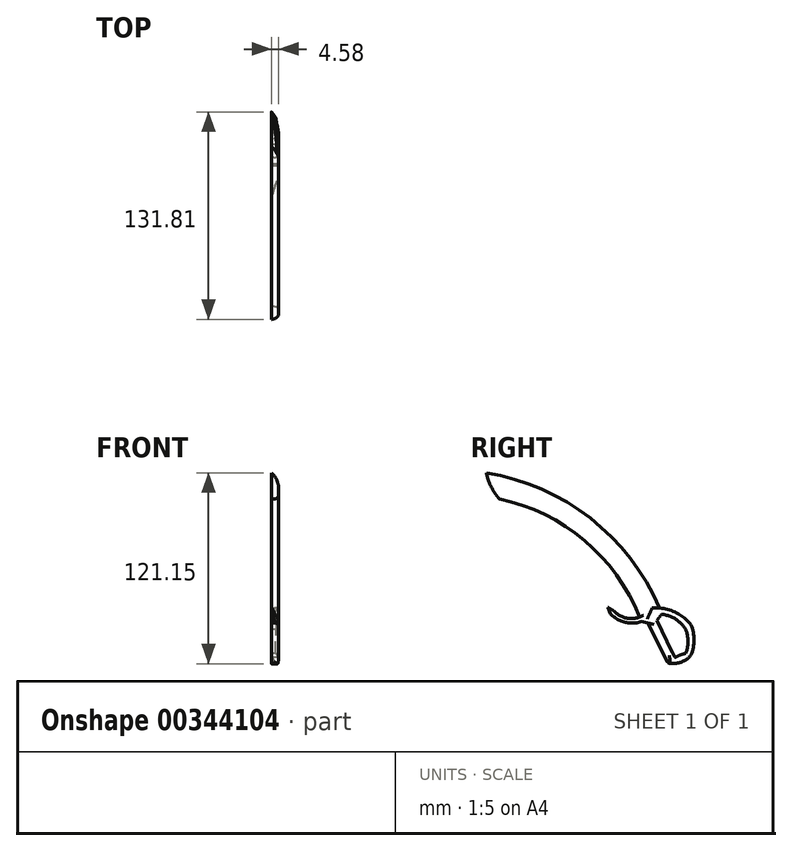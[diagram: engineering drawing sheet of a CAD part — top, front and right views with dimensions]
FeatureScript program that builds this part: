
annotation { "Feature Type Name" : "Feature", "Feature Type Description" : "" }
export const myFeature = defineFeature(function(context is Context, id is Id, definition is map)
    precondition{}
    {
        {
            var Q0;
            Q0=qCreatedBy(makeId("Right.planeOp"),FACE);
            var sketch = newSketch(context, id + "F0", { "sketchPlane" : qUnion([Q0])});
            skArc(sketch, "E0", {"start": v(55.77, -25.1) * mm, "mid": v(11.84, 31.93) * mm, "end": v(-54.16, 60.68) * mm});
            skArc(sketch, "E1", {"start": v(43.15, -30.87) * mm, "mid": v(8.04, 17.8) * mm, "end": v(-45.88, 44.15) * mm});
            skArc(sketch, "E2", {"start": v(26.88, -27.02) * mm, "mid": v(34.43, -31.4) * mm, "end": v(43.15, -30.87) * mm});
            skArc(sketch, "E3", {"start": v(24.68, -28.79) * mm, "mid": v(33.82, -34.17) * mm, "end": v(44.41, -33.72) * mm});
            skLineSegment(sketch, "E4", {"start": v(44.41, -33.72) * mm, "end": v(48.52, -34.67) * mm});
            skLineSegment(sketch, "E5", {"start": v(48.52, -34.67) * mm, "end": v(60.52, -58.92) * mm});
            skLineSegment(sketch, "E6", {"start": v(57.04, -29.15) * mm, "end": v(54.22, -32.9) * mm});
            skLineSegment(sketch, "E7", {"start": v(54.22, -32.9) * mm, "end": v(65.62, -56.63) * mm});
            skLineSegment(sketch, "E8", {"start": v(24.68, -28.79) * mm, "end": v(23.2, -24.76) * mm});
            skLineSegment(sketch, "E9", {"start": v(23.2, -24.76) * mm, "end": v(26.88, -27.02) * mm});
            skArc(sketch, "E10", {"start": v(60.52, -58.92) * mm, "mid": v(64.17, -60.23) * mm, "end": v(65.62, -56.63) * mm});
            skArc(sketch, "E11", {"start": v(-54.16, 60.68) * mm, "mid": v(-51.15, 51.85) * mm, "end": v(-45.88, 44.15) * mm});
            skArc(sketch, "E12", {"start": v(49.46, -27.99) * mm, "mid": v(8.46, 23.66) * mm, "end": v(-51.15, 51.85) * mm});
            skLineSegment(sketch, "E13", {"start": v(55.77, -25.1) * mm, "end": v(43.15, -30.87) * mm});
            skArc(sketch, "E14", {"start": v(72.45, -38.84) * mm, "mid": v(65.93, -32.1) * mm, "end": v(57.04, -29.15) * mm});
            skArc(sketch, "E15", {"start": v(75.83, -35.91) * mm, "mid": v(66.96, -28.37) * mm, "end": v(55.77, -25.1) * mm});
            skArc(sketch, "E16", {"start": v(72.45, -53.95) * mm, "mid": v(73.9, -46.4) * mm, "end": v(72.45, -38.84) * mm});
            skArc(sketch, "E17", {"start": v(75.83, -54.86) * mm, "mid": v(77.65, -45.39) * mm, "end": v(75.83, -35.91) * mm});
            skArc(sketch, "E18", {"start": v(72.45, -53.95) * mm, "mid": v(68.92, -55) * mm, "end": v(65.62, -56.63) * mm});
            skArc(sketch, "E19", {"start": v(64.17, -60.23) * mm, "mid": v(70.68, -59.01) * mm, "end": v(75.83, -54.86) * mm});
            skSolve(sketch);
        }
        {
            var Q0;
            {var subQ0=sQuery(id+"F0.wireOp",EDGE,"E1");Q0=makeQuery(id+"F0.imprint","IMPRINT",FACE,{"disambiguationData":[TD([[makeQuery(id+"F0.imprint","IMPRINT",EDGE,{"derivedFrom":subQ0}),-1.0]])]});}
            var Q1;
            {var subQ0=sQuery(id+"F0.wireOp",EDGE,"E0");Q1=makeQuery(id+"F0.imprint","IMPRINT",FACE,{"disambiguationData":[TD([[makeQuery(id+"F0.imprint","IMPRINT",EDGE,{"derivedFrom":subQ0}),1.0]])]});}
            var Q2;
            {var subQ3=sQuery(id+"F0.wireOp",EDGE,"E2");Q2=makeQuery(id+"F0.imprint","IMPRINT",FACE,{"disambiguationData":[TD([[makeQuery(id+"F0.imprint","IMPRINT",EDGE,{"derivedFrom":subQ3}),-1.0]])]});}
            extrude(context, id + "F1", {"entities" : qUnion([Q0, Q1, Q2]), "endBound" : BoundingType.SYMMETRIC, "depth" : 4.57 * mm});
        }
        {
            var Q0;
            Q0=makeQuery(id+"F1.opExtrude","CAP_EDGE",EDGE,{"disambiguationData":[OSD([sQuery(id+"F0.wireOp",EDGE,"E0")])],"isStart":false});
            fillet(context, id + "F2", {"entities" : qUnion([Q0]), "radius" : 12.7 * mm, "tangentPropagation" : true, "allowEdgeOverflow" : false});
        }
        {
            var Q0;
            Q0=makeQuery(id+"F1.opExtrude","CAP_EDGE",EDGE,{"disambiguationData":[OSD([sQuery(id+"F0.wireOp",EDGE,"E1")])],"isStart":false});
            fillet(context, id + "F3", {"entities" : qUnion([Q0]), "radius" : 2.54 * mm, "tangentPropagation" : true, "allowEdgeOverflow" : false});
        }
        {
            var Q0;
            Q0=makeQuery(id+"F1.opExtrude","CAP_EDGE",EDGE,{"disambiguationData":[OSD([sQuery(id+"F0.wireOp",EDGE,"E5")])],"isStart":false});
            fillet(context, id + "F4", {"entities" : qUnion([Q0]), "radius" : 3.07 * mm, "tangentPropagation" : true, "allowEdgeOverflow" : false});
        }
        {
            var Q0;
            Q0=makeQuery(id+"F1.opExtrude","CAP_EDGE",EDGE,{"disambiguationData":[OSD([sQuery(id+"F0.wireOp",EDGE,"E8")])],"isStart":false});
            fillet(context, id + "F5", {"entities" : qUnion([Q0]), "radius" : 32.5 * mm, "tangentPropagation" : true, "allowEdgeOverflow" : false});
        }
        {
            var Q0;
            Q0=makeQuery(id+"F1.opExtrude","CAP_EDGE",EDGE,{"disambiguationData":[OSD([sQuery(id+"F0.wireOp",EDGE,"E17")])],"isStart":false});
            fillet(context, id + "F6", {"entities" : qUnion([Q0]), "radius" : 17.17 * mm, "tangentPropagation" : true, "allowEdgeOverflow" : false});
        }
    });
